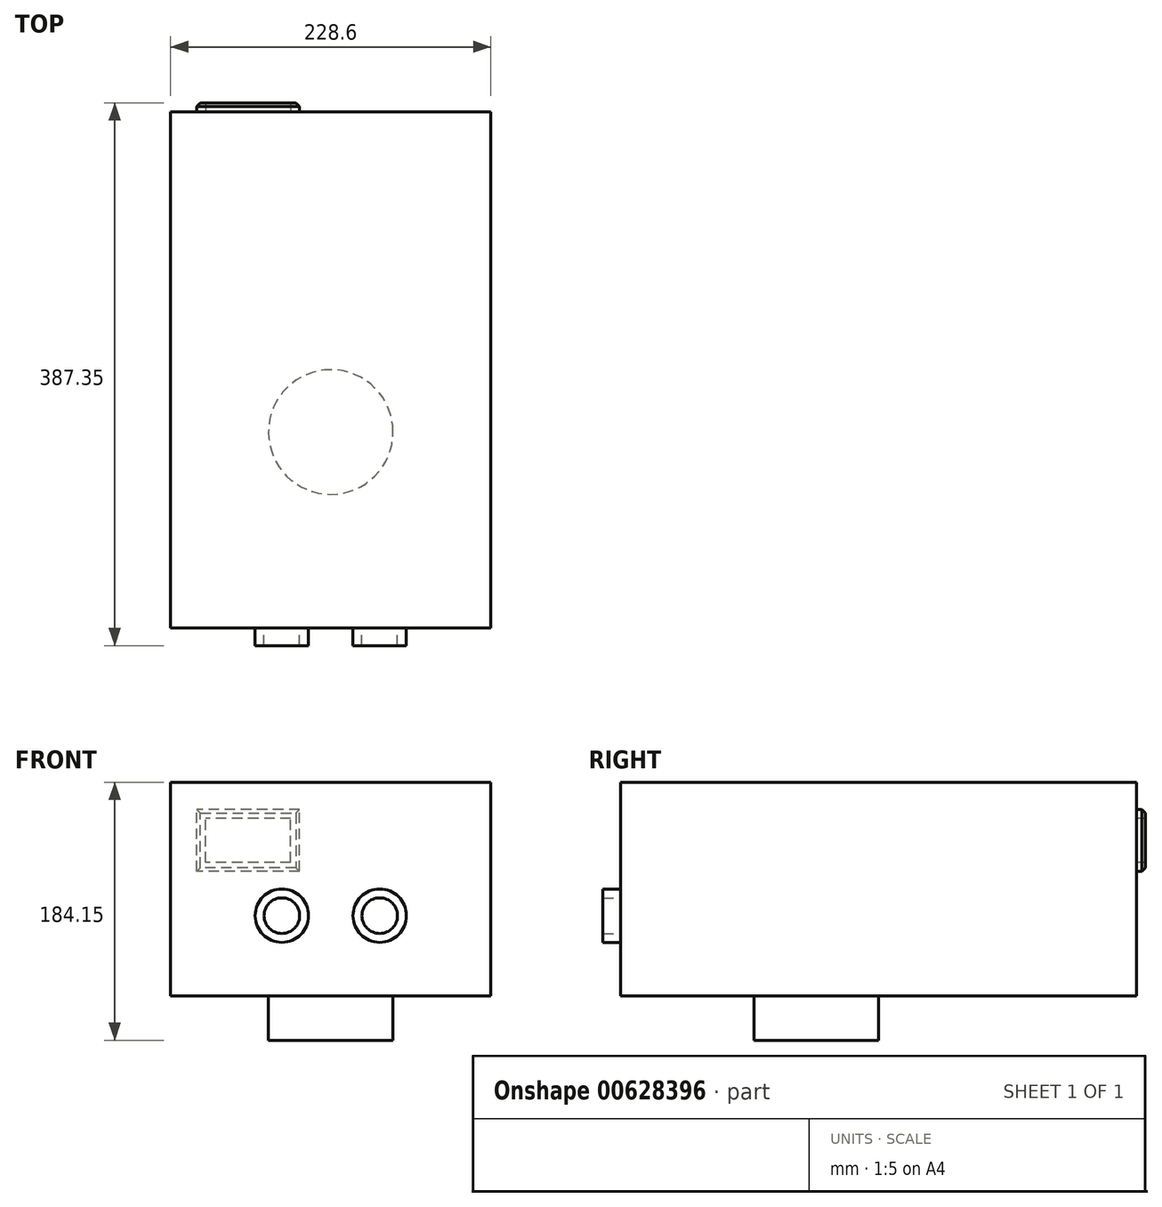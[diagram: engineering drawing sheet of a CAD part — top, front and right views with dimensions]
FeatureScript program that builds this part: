
annotation { "Feature Type Name" : "Feature", "Feature Type Description" : "" }
export const myFeature = defineFeature(function(context is Context, id is Id, definition is map)
    precondition{}
    {
        {
            var Q0;
            Q0=qCreatedBy(makeId("Top.planeOp"),FACE);
            var sketch = newSketch(context, id + "F0", { "sketchPlane" : qUnion([Q0])});
            skLineSegment(sketch, "E0", {"start": v(0, 0) * mm, "end": v(0, 228.6) * mm});
            skLineSegment(sketch, "E1", {"start": v(0, 228.6) * mm, "end": v(114.3, 228.6) * mm});
            skLineSegment(sketch, "E2", {"start": v(0, 0) * mm, "end": v(0, -139.7) * mm});
            skLineSegment(sketch, "E3", {"start": v(0, -139.7) * mm, "end": v(-114.3, -139.7) * mm});
            skCircle(sketch, "E4", {"center": v(0, 0) * mm, "radius": 44.45 * mm});
            skLineSegment(sketch, "E5.bottom", {"start": v(114.3, 228.6) * mm, "end": v(-114.3, 228.6) * mm});
            skLineSegment(sketch, "E5.top", {"start": v(114.3, -139.7) * mm, "end": v(-114.3, -139.7) * mm});
            skLineSegment(sketch, "E5.left", {"start": v(114.3, 228.6) * mm, "end": v(114.3, -139.7) * mm});
            skLineSegment(sketch, "E5.right", {"start": v(-114.3, 228.6) * mm, "end": v(-114.3, -139.7) * mm});
            skSolve(sketch);
        }
        {
            var Q0;
            {var subQ4=sQuery(id+"FMQ4oYpifHlsS3X_0.wireOp",EDGE,"2200b648-bf06-4f91-9637-0e87c0684983");var subQ8=sQuery(id+"FMQ4oYpifHlsS3X_0.wireOp",EDGE,"b89c08a9-1273-4d7e-b56b-5360fc8114ab.left");var subQ9=makeQuery(id+"FMQ4oYpifHlsS3X_0.imprint","INTERSECT",VERTEX,{"derivedFrom":[subQ4,subQ8]});Q0=makeQuery(id+"FMQ4oYpifHlsS3X_0.imprint","IMPRINT",FACE,{"disambiguationData":[TD([[makeQuery(id+"FMQ4oYpifHlsS3X_0.imprint","IMPRINT",EDGE,{"disambiguationData":[TD([[subQ9,1.0]])],"derivedFrom":subQ4}),-1.0]])]});}
            var Q1;
            {var subQ1=sQuery(id+"FMQ4oYpifHlsS3X_0.wireOp",EDGE,"2200b648-bf06-4f91-9637-0e87c0684983");var subQ7=sQuery(id+"FMQ4oYpifHlsS3X_0.wireOp",EDGE,"b89c08a9-1273-4d7e-b56b-5360fc8114ab.left");var subQ9=makeQuery(id+"FMQ4oYpifHlsS3X_0.imprint","INTERSECT",VERTEX,{"derivedFrom":[subQ1,subQ7]});Q1=makeQuery(id+"FMQ4oYpifHlsS3X_0.imprint","IMPRINT",FACE,{"disambiguationData":[TD([[makeQuery(id+"FMQ4oYpifHlsS3X_0.imprint","IMPRINT",EDGE,{"disambiguationData":[TD([[subQ9,1.0]])],"derivedFrom":subQ1}),1.0]])]});}
            var Q2;
            {var subQ3=sQuery(id+"FMQ4oYpifHlsS3X_0.wireOp",EDGE,"b89c08a9-1273-4d7e-b56b-5360fc8114ab.right");Q2=makeQuery(id+"FMQ4oYpifHlsS3X_0.imprint","IMPRINT",FACE,{"disambiguationData":[TD([[makeQuery(id+"FMQ4oYpifHlsS3X_0.imprint","IMPRINT",EDGE,{"derivedFrom":subQ3}),1.0]])]});}
            var Q3;
            {var subQ1=sQuery(id+"FMQ4oYpifHlsS3X_0.wireOp",EDGE,"c8c8b09a-aff6-4b6d-9523-402620295f6a");var subQ3=sQuery(id+"FMQ4oYpifHlsS3X_0.wireOp",EDGE,"7282fe88-ce41-4641-b3ac-2da0a1dd6b1d");var subQ4=makeQuery(id+"FMQ4oYpifHlsS3X_0.imprint","INTERSECT",VERTEX,{"derivedFrom":[subQ1,subQ3]});Q3=makeQuery(id+"FMQ4oYpifHlsS3X_0.imprint","IMPRINT",FACE,{"disambiguationData":[TD([[makeQuery(id+"FMQ4oYpifHlsS3X_0.imprint","IMPRINT",EDGE,{"disambiguationData":[TD([[subQ4,-1.0]])],"derivedFrom":subQ3}),1.0]])]});}
            var Q4;
            {var subQ1=sQuery(id+"FMQ4oYpifHlsS3X_0.wireOp",EDGE,"2200b648-bf06-4f91-9637-0e87c0684983");var subQ3=sQuery(id+"FMQ4oYpifHlsS3X_0.wireOp",EDGE,"7282fe88-ce41-4641-b3ac-2da0a1dd6b1d");var subQ4=makeQuery(id+"FMQ4oYpifHlsS3X_0.imprint","INTERSECT",VERTEX,{"derivedFrom":[subQ1,subQ3]});Q4=makeQuery(id+"FMQ4oYpifHlsS3X_0.imprint","IMPRINT",FACE,{"disambiguationData":[TD([[makeQuery(id+"FMQ4oYpifHlsS3X_0.imprint","IMPRINT",EDGE,{"disambiguationData":[TD([[subQ4,-1.0]])],"derivedFrom":subQ3}),1.0]])]});}
            var Q5;
            {var subQ0=sQuery(id+"FMQ4oYpifHlsS3X_0.wireOp",EDGE,"dc3a1fce-f40b-4095-96dd-6cae36510fd4");Q5=makeQuery(id+"FMQ4oYpifHlsS3X_0.imprint","IMPRINT",FACE,{"disambiguationData":[TD([[makeQuery(id+"FMQ4oYpifHlsS3X_0.imprint","IMPRINT",EDGE,{"derivedFrom":subQ0}),-1.0]])]});}
            var Q6;
            {var subQ0=sQuery(id+"FMQ4oYpifHlsS3X_0.wireOp",EDGE,"dc3a1fce-f40b-4095-96dd-6cae36510fd4");Q6=makeQuery(id+"FMQ4oYpifHlsS3X_0.imprint","IMPRINT",FACE,{"disambiguationData":[TD([[makeQuery(id+"FMQ4oYpifHlsS3X_0.imprint","IMPRINT",EDGE,{"derivedFrom":subQ0}),1.0]])]});}
            var Q7;
            {var subQ11=sQuery(id+"FMQ4oYpifHlsS3X_0.wireOp",EDGE,"b89c08a9-1273-4d7e-b56b-5360fc8114ab.left");Q7=makeQuery(id+"FMQ4oYpifHlsS3X_0.imprint","IMPRINT",FACE,{"disambiguationData":[TD([[makeQuery(id+"FMQ4oYpifHlsS3X_0.imprint","IMPRINT",EDGE,{"derivedFrom":subQ11}),-1.0]])]});}
            var Q8;
            {var subQ9=sQuery(id+"F0.wireOp",EDGE,"E5.left");Q8=makeQuery(id+"F0.imprint","IMPRINT",FACE,{"disambiguationData":[TD([[makeQuery(id+"F0.imprint","IMPRINT",EDGE,{"derivedFrom":subQ9}),-1.0]])]});}
            var Q9;
            {var subQ3=sQuery(id+"F0.wireOp",EDGE,"E5.right");Q9=makeQuery(id+"F0.imprint","IMPRINT",FACE,{"disambiguationData":[TD([[makeQuery(id+"F0.imprint","IMPRINT",EDGE,{"derivedFrom":subQ3}),1.0]])]});}
            var Q10;
            {var subQ0=sQuery(id+"F0.wireOp",EDGE,"E2");var subQ1=sQuery(id+"F0.wireOp",EDGE,"E0");var subQ2=makeQuery(id+"F0.imprint","INTERSECT",VERTEX,{"derivedFrom":[subQ1,subQ0]});Q10=makeQuery(id+"F0.imprint","IMPRINT",FACE,{"disambiguationData":[TD([[makeQuery(id+"F0.imprint","IMPRINT",EDGE,{"disambiguationData":[TD([[subQ2,-1.0]])],"derivedFrom":subQ1}),-1.0]])]});}
            var Q11;
            {var subQ0=sQuery(id+"F0.wireOp",EDGE,"E2");var subQ1=sQuery(id+"F0.wireOp",EDGE,"E0");var subQ2=makeQuery(id+"F0.imprint","INTERSECT",VERTEX,{"derivedFrom":[subQ1,subQ0]});Q11=makeQuery(id+"F0.imprint","IMPRINT",FACE,{"disambiguationData":[TD([[makeQuery(id+"F0.imprint","IMPRINT",EDGE,{"disambiguationData":[TD([[subQ2,-1.0]])],"derivedFrom":subQ1}),1.0]])]});}
            extrude(context, id + "F1", {"entities" : qUnion([Q0, Q1, Q2, Q3, Q4, Q5, Q6, Q7, Q8, Q9, Q10, Q11]), "depth" : 152.4 * mm, "offsetDistance" : 25.4 * mm});
        }
        {
            var Q0;
            {var subQ0=sQuery(id+"F0.wireOp",EDGE,"E2");var subQ1=sQuery(id+"F0.wireOp",EDGE,"E0");var subQ2=makeQuery(id+"F0.imprint","INTERSECT",VERTEX,{"derivedFrom":[subQ1,subQ0]});Q0=makeQuery(id+"F0.imprint","IMPRINT",FACE,{"disambiguationData":[TD([[makeQuery(id+"F0.imprint","IMPRINT",EDGE,{"disambiguationData":[TD([[subQ2,-1.0]])],"derivedFrom":subQ1}),-1.0]])]});}
            var Q1;
            {var subQ0=sQuery(id+"F0.wireOp",EDGE,"E2");var subQ1=sQuery(id+"F0.wireOp",EDGE,"E0");var subQ2=makeQuery(id+"F0.imprint","INTERSECT",VERTEX,{"derivedFrom":[subQ1,subQ0]});Q1=makeQuery(id+"F0.imprint","IMPRINT",FACE,{"disambiguationData":[TD([[makeQuery(id+"F0.imprint","IMPRINT",EDGE,{"disambiguationData":[TD([[subQ2,-1.0]])],"derivedFrom":subQ1}),1.0]])]});}
            extrude(context, id + "F2", {"entities" : qUnion([Q0, Q1]), "operationType" : NewBodyOperationType.ADD, "oppositeDirection" : true, "depth" : 31.75 * mm, "offsetDistance" : 25.4 * mm});
        }
        {
            var Q0;
            Q0=makeQuery(id+"F1.opExtrude","SWEPT_FACE",FACE,{"disambiguationData":[OSD([sQuery(id+"F0.wireOp",EDGE,"E5.bottom")])]});
            var sketch = newSketch(context, id + "F3", { "sketchPlane" : qUnion([Q0])});
            skLineSegment(sketch, "E6.bottom", {"start": v(28.62, 95.16) * mm, "end": v(89.31, 95.16) * mm});
            skLineSegment(sketch, "E6.top", {"start": v(28.62, 126.4) * mm, "end": v(89.31, 126.4) * mm});
            skLineSegment(sketch, "E6.left", {"start": v(28.62, 95.16) * mm, "end": v(28.62, 126.4) * mm});
            skLineSegment(sketch, "E6.right", {"start": v(89.31, 95.16) * mm, "end": v(89.31, 126.4) * mm});
            skLineSegment(sketch, "E7.0", {"start": v(22.27, 88.81) * mm, "end": v(95.66, 88.81) * mm});
            skLineSegment(sketch, "E7.1", {"start": v(22.27, 88.81) * mm, "end": v(22.27, 132.75) * mm});
            skLineSegment(sketch, "E7.2", {"start": v(22.27, 132.75) * mm, "end": v(95.66, 132.75) * mm});
            skLineSegment(sketch, "E7.3", {"start": v(95.66, 88.81) * mm, "end": v(95.66, 132.75) * mm});
            skSolve(sketch);
        }
        {
            var Q0;
            Q0=makeQuery(id+"FokMA0W8opQbB1W_1.imprint","IMPRINT",FACE,{"disambiguationData":[TD([[makeQuery(id+"FokMA0W8opQbB1W_1.imprint","IMPRINT",EDGE,{"derivedFrom":sQuery(id+"FokMA0W8opQbB1W_1.wireOp",EDGE,"7acc4ab9-38d1-4ac3-9c39-dab9b0dd8841.bottom")}),1.0]])]});
            var Q1;
            Q1=makeQuery(id+"F3.imprint","IMPRINT",FACE,{"disambiguationData":[TD([[makeQuery(id+"F3.imprint","IMPRINT",EDGE,{"derivedFrom":sQuery(id+"F3.wireOp",EDGE,"E6.bottom")}),-1.0]])]});
            extrude(context, id + "F4", {"entities" : qUnion([Q0, Q1]), "operationType" : NewBodyOperationType.ADD, "depth" : 6.35 * mm, "offsetDistance" : 25.4 * mm});
        }
        {
            var Q0;
            Q0=makeQuery(id+"F4.opExtrude","CAP_EDGE",EDGE,{"disambiguationData":[OSD([sQuery(id+"F3.wireOp",EDGE,"E7.3")])],"isStart":false});
            var Q1;
            Q1=makeQuery(id+"F4.opExtrude","CAP_EDGE",EDGE,{"disambiguationData":[OSD([sQuery(id+"F3.wireOp",EDGE,"E7.0")])],"isStart":false});
            var Q2;
            Q2=makeQuery(id+"F4.opExtrude","CAP_EDGE",EDGE,{"disambiguationData":[OSD([sQuery(id+"F3.wireOp",EDGE,"E7.1")])],"isStart":false});
            var Q3;
            Q3=makeQuery(id+"F4.opExtrude","CAP_EDGE",EDGE,{"disambiguationData":[OSD([sQuery(id+"F3.wireOp",EDGE,"E7.2")])],"isStart":false});
            chamfer(context, id + "F5", {"entities" : qUnion([Q0, Q1, Q2, Q3]), "width" : 2.54 * mm, "tangentPropagation" : true});
        }
        {
            var Q0;
            Q0=makeQuery(id+"F1.opExtrude","SWEPT_FACE",FACE,{"disambiguationData":[OSD([sQuery(id+"F0.wireOp",EDGE,"E5.top")])]});
            var sketch = newSketch(context, id + "F6", { "sketchPlane" : qUnion([Q0])});
            skLineSegment(sketch, "E8", {"start": v(0, 0) * mm, "end": v(0, 57.15) * mm});
            skLineSegment(sketch, "E9", {"start": v(0, 57.15) * mm, "end": v(34.92, 57.15) * mm});
            skLineSegment(sketch, "E10", {"start": v(0, 57.15) * mm, "end": v(-34.93, 57.15) * mm});
            skCircle(sketch, "E11", {"center": v(34.92, 57.15) * mm, "radius": 12.7 * mm});
            skCircle(sketch, "E12", {"center": v(-34.93, 57.15) * mm, "radius": 12.7 * mm});
            skCircle(sketch, "E13.0", {"center": v(34.92, 57.15) * mm, "radius": 19.05 * mm});
            skCircle(sketch, "E14.0", {"center": v(-34.93, 57.15) * mm, "radius": 19.05 * mm});
            skSolve(sketch);
        }
        {
            var Q0;
            Q0=makeQuery(id+"F6.imprint","IMPRINT",FACE,{"disambiguationData":[TD([[makeQuery(id+"F6.imprint","IMPRINT",EDGE,{"derivedFrom":sQuery(id+"F6.wireOp",EDGE,"E11")}),-1.0]])]});
            var Q1;
            Q1=makeQuery(id+"F6.imprint","IMPRINT",FACE,{"disambiguationData":[TD([[makeQuery(id+"F6.imprint","IMPRINT",EDGE,{"derivedFrom":sQuery(id+"F6.wireOp",EDGE,"E12")}),-1.0]])]});
            extrude(context, id + "F7", {"entities" : qUnion([Q0, Q1]), "operationType" : NewBodyOperationType.ADD, "depth" : 12.7 * mm, "offsetDistance" : 25.4 * mm});
        }
    });
